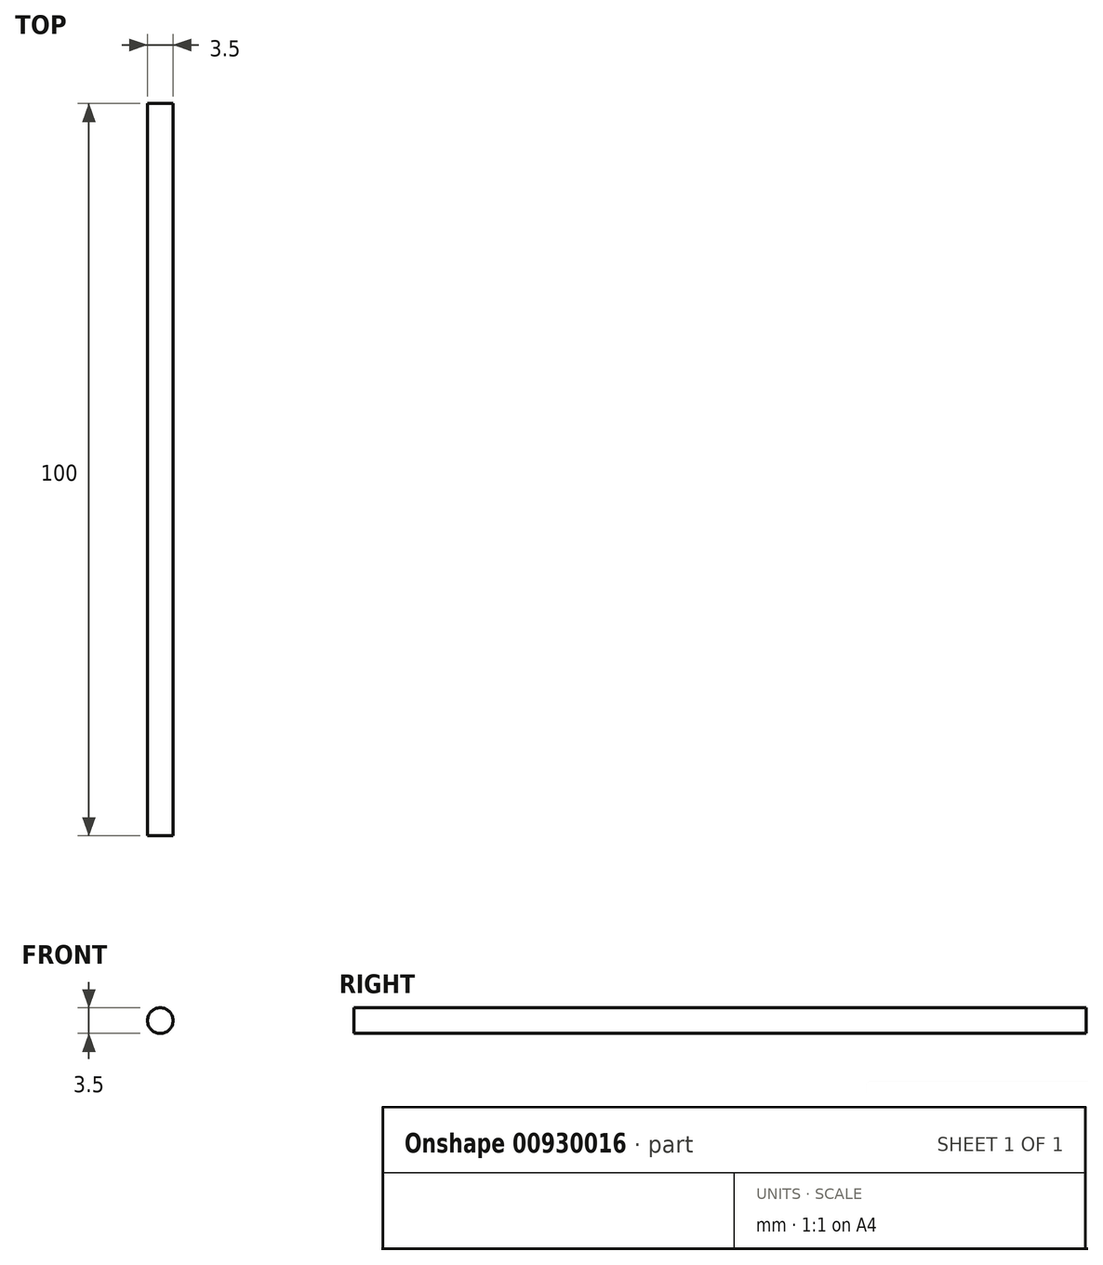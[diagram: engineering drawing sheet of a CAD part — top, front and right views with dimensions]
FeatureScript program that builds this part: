
annotation { "Feature Type Name" : "Feature", "Feature Type Description" : "" }
export const myFeature = defineFeature(function(context is Context, id is Id, definition is map)
    precondition{}
    {
        {
            var Q0;
            Q0=qCreatedBy(makeId("Front.planeOp"),FACE);
            var sketch = newSketch(context, id + "F0", { "sketchPlane" : qUnion([Q0])});
            skCircle(sketch, "E0", {"center": v(0, 0) * mm, "radius": 1.75 * mm});
            skSolve(sketch);
        }
        {
            var Q0;
            Q0 = qSketchRegion(id + "F0", true);
            extrude(context, id + "F1", {"entities" : qUnion([Q0]), "depth" : 100 * mm, "offsetDistance" : 25.4 * mm});
        }
    });
